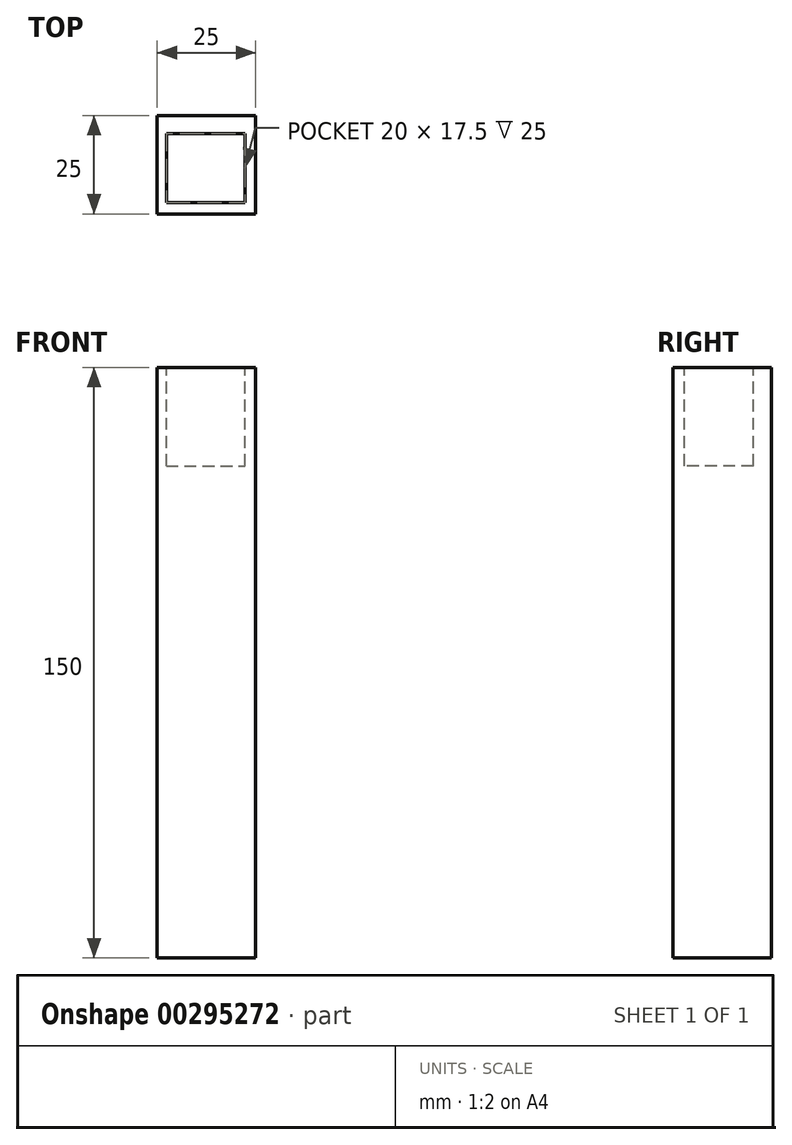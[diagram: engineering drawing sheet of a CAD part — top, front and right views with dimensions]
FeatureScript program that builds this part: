
annotation { "Feature Type Name" : "Feature", "Feature Type Description" : "" }
export const myFeature = defineFeature(function(context is Context, id is Id, definition is map)
    precondition{}
    {
        {
            var Q0;
            Q0=qCreatedBy(makeId("Front.planeOp"),FACE);
            var sketch = newSketch(context, id + "F0", { "sketchPlane" : qUnion([Q0])});
            skLineSegment(sketch, "E0.bottom", {"start": v(0, 0) * mm, "end": v(25, 0) * mm});
            skLineSegment(sketch, "E0.top", {"start": v(0, 150) * mm, "end": v(25, 150) * mm});
            skLineSegment(sketch, "E0.left", {"start": v(0, 0) * mm, "end": v(0, 150) * mm});
            skLineSegment(sketch, "E0.right", {"start": v(25, 0) * mm, "end": v(25, 150) * mm});
            skSolve(sketch);
        }
        {
            var Q0;
            Q0=qSketchRegion(id+"F0",true);
            extrude(context, id + "F1", {"entities" : qUnion([Q0]), "depth" : 25 * mm});
        }
        {
            var Q0;
            Q0=makeQuery(id+"F1.opExtrude","SWEPT_FACE",FACE,{"disambiguationData":[OSD([sQuery(id+"F0.wireOp",EDGE,"E0.top")])]});
            var sketch = newSketch(context, id + "F2", { "sketchPlane" : qUnion([Q0])});
            skLineSegment(sketch, "E1.bottom", {"start": v(2.32, -4.58) * mm, "end": v(22.32, -4.58) * mm});
            skLineSegment(sketch, "E1.top", {"start": v(2.32, -22.08) * mm, "end": v(22.32, -22.08) * mm});
            skLineSegment(sketch, "E1.left", {"start": v(2.32, -4.58) * mm, "end": v(2.32, -22.08) * mm});
            skLineSegment(sketch, "E1.right", {"start": v(22.32, -4.58) * mm, "end": v(22.32, -22.08) * mm});
            skSolve(sketch);
        }
        {
            var Q0;
            Q0=qSketchRegion(id+"F2",true);
            extrude(context, id + "F3", {"entities" : qUnion([Q0]), "operationType" : NewBodyOperationType.REMOVE, "oppositeDirection" : true, "depth" : 25 * mm});
        }
    });
